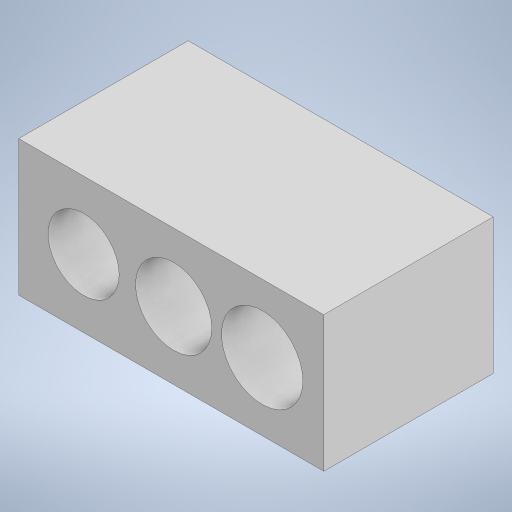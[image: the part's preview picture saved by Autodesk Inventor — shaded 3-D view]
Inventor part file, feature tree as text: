
AUTODESK INVENTOR PART (.ipt)
format: ipt  version: 2023 (Build 270158000, 158)  size: 264,704 bytes
history: native  units: in
note: dims shown in document units (in); Inventor stores cm internally (conversion verified against a paired STEP export)
features: extrude x1, sketch x1
ambient origin geometry x8: Origin, YZ Plane, XZ Plane, XY Plane, X Axis, Y Axis, Z Axis, Center Point
bodies: Body1 (feature_tree)
feature tree (2):
  extrude  "Extrusion4"  Depth=0.315in
  sketch  "Sketch6"  dims[d11=0.7087in d12=0.315in d13=0.1654in d14=0.1772in d15=0.189in d16=0.3937in d17=0.0in]
